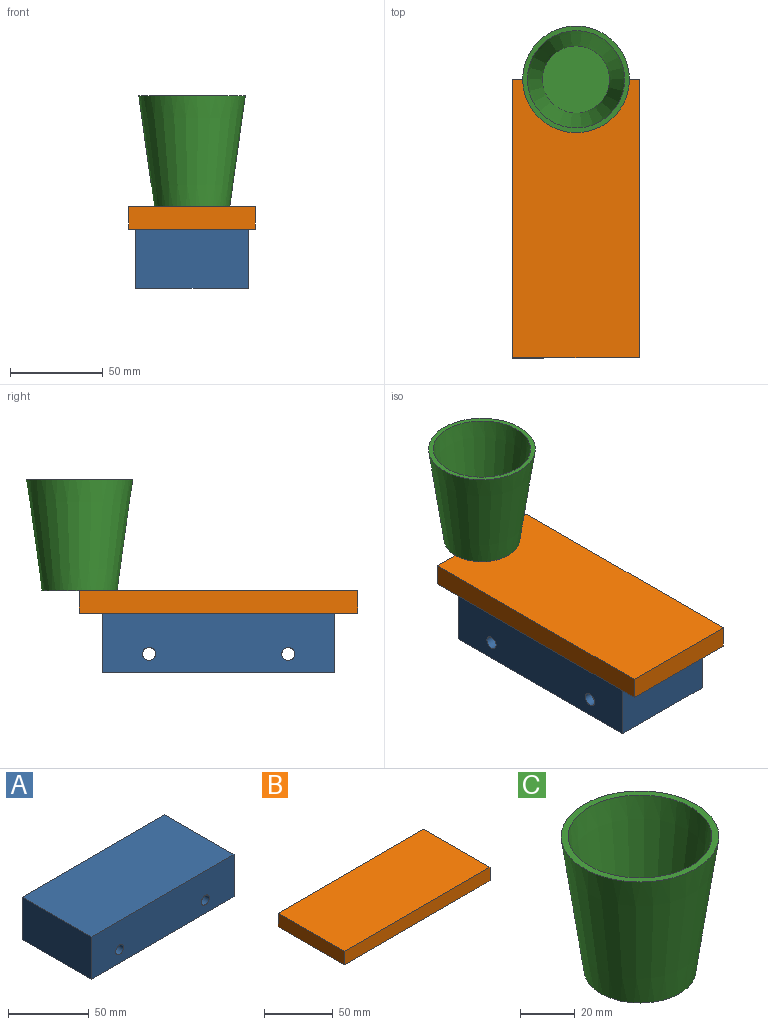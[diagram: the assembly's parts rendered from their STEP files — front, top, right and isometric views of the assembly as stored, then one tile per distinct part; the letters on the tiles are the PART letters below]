
ASSEMBLY  parts=3 mates=2
PART A: 8 faces, bbox 125x60.4x32 mm
  f0: plane 60.4x32mm, normal (1,0,0), area 1932.8mm2, adj f1,f4,f6,f7
  f1: plane 125x60.4mm, normal (0,0,1), area 7550mm2, adj f0,f2,f6,f7
  f2: plane 60.4x32mm, normal (-1,0,0), area 1932.8mm2, adj f1,f4,f6,f7
  f3: cylinder r=3.5mm len=60.4mm, axis (0,1,0), area 1328.3mm2, adj f6,f7
  f4: plane 125x60.4mm, normal (0,0,-1), area 7550mm2, adj f0,f2,f6,f7
  f5: cylinder r=3.5mm len=60.4mm, axis (0,1,0), area 1328.3mm2, adj f6,f7
  f6: plane 125x32mm, normal (0,1,0), area 3923mm2, adj f0,f1,f2,f3,f4,f5
  f7: plane 125x32mm, normal (0,-1,0), area 3923mm2, adj f0,f1,f2,f3,f4,f5
PART B: 6 faces, bbox 150x68x12 mm
  f0: plane 150x12mm, normal (0,1,0), area 1800mm2, adj f1,f3,f4,f5
  f1: plane 68x12mm, normal (-1,0,0), area 816mm2, adj f0,f2,f4,f5
  f2: plane 150x12mm, normal (0,-1,0), area 1800mm2, adj f1,f3,f4,f5
  f3: plane 68x12mm, normal (1,0,0), area 816mm2, adj f0,f2,f4,f5
  f4: plane 150x68mm, normal (0,0,1), area 10200mm2, adj f0,f1,f2,f3
  f5: plane 150x68mm, normal (0,0,-1), area 10200mm2, adj f0,f1,f2,f3
PART C: 5 faces, bbox 57.5x57.5x59.9 mm
  f0: cone r=20.33mm half-angle=8deg, axis (0,0,1), area 9333mm2, adj f1,f2
  f1: plane 57.5x57.5mm, normal (0,0,1), area 442.7mm2, adj f0,f3
  f2: plane 40.65x40.65mm, normal (0,0,-1), area 1298mm2, adj f0
  f3: cone r=17.81mm half-angle=8deg, axis (0,0,1), area 8068.3mm2, adj f1,f4
  f4: plane 36.24x36.24mm, normal (0,0,1), area 1031.3mm2, adj f3
PLACE A rot(axis=(0,0,-1),90deg) t=(-9.17,-93.18,-43.83)mm
PLACE B rot(axis=(0,0,-1),90deg) t=(-39.57,-27.21,-11.83)mm
PLACE C t=(27.86,-6.42,0.17)mm
MATE fastened C.f0 <-> B.f4  axis (0,0,1) through (-39.37,44.32,0.17)mm
MATE fastened A.f1 <-> B.f5  axis (0,0,1) through (-39.37,-30.68,-11.83)mm
